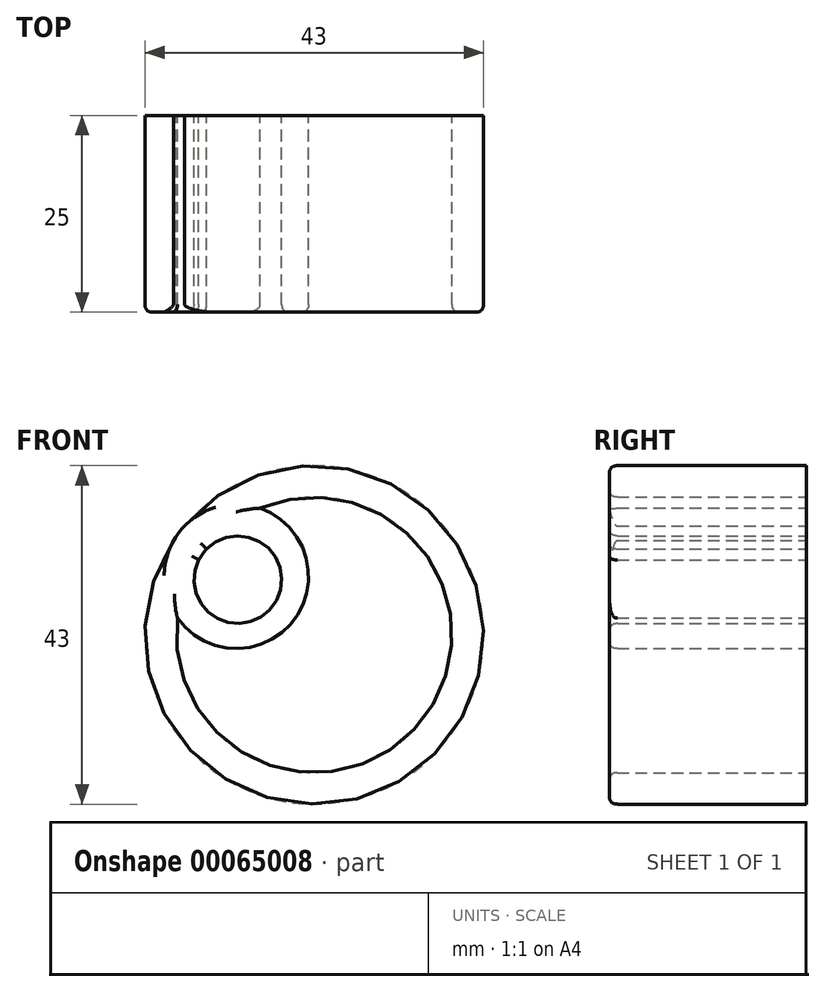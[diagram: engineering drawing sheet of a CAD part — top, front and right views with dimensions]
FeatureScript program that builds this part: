
annotation { "Feature Type Name" : "Feature", "Feature Type Description" : "" }
export const myFeature = defineFeature(function(context is Context, id is Id, definition is map)
    precondition{}
    {
        {
            var Q0;
            Q0=qCreatedBy(makeId("Front.planeOp"),FACE);
            var sketch = newSketch(context, id + "F0", { "sketchPlane" : qUnion([Q0])});
            skCircle(sketch, "E0", {"center": v(0, 0) * mm, "radius": 21.5 * mm});
            skCircle(sketch, "E1", {"center": v(0, 0) * mm, "radius": 17.5 * mm});
            skSolve(sketch);
        }
        {
            var Q0;
            Q0 = qSketchRegion(id + "F0", true);
            extrude(context, id + "F1", {"entities" : qUnion([Q0]), "depth" : 25 * mm});
        }
        {
            var Q0;
            Q0=qCreatedBy(makeId("Front.planeOp"),FACE);
            var sketch = newSketch(context, id + "F2", { "sketchPlane" : qUnion([Q0])});
            skCircle(sketch, "E2", {"center": v(-9.89, 7.43) * mm, "radius": 9.17 * mm});
            skPoint(sketch, "E2.first.point", {"position": v(-16.92, 13.32) * mm});
            skPoint(sketch, "E2.second.point", {"position": v(-1.16, 4.61) * mm});
            skPoint(sketch, "E2.third.point", {"position": v(-1.05, 4.98) * mm});
            skCircle(sketch, "E3", {"center": v(-9.7, 7.01) * mm, "radius": 5.57 * mm});
            skPoint(sketch, "E3.first.point", {"position": v(-14.32, 10.14) * mm});
            skPoint(sketch, "E3.second.point", {"position": v(-4.83, 4.31) * mm});
            skPoint(sketch, "E3.third.point", {"position": v(-4.24, 5.95) * mm});
            skSolve(sketch);
        }
        {
            var Q0;
            Q0 = qSketchRegion(id + "F2", true);
            extrude(context, id + "F3", {"entities" : qUnion([Q0]), "operationType" : NewBodyOperationType.ADD, "depth" : 25 * mm});
        }
        {
            var Q0;
            Q0=qCreatedBy(makeId("Front.planeOp"),FACE);
            var sketch = newSketch(context, id + "F4", { "sketchPlane" : qUnion([Q0])});
            skCircle(sketch, "E4", {"center": v(9.71, 7.92) * mm, "radius": 8.9 * mm});
            skPoint(sketch, "E4.first.point", {"position": v(15.77, 14.45) * mm});
            skPoint(sketch, "E4.second.point", {"position": v(4.3, 0.85) * mm});
            skPoint(sketch, "E4.third.point", {"position": v(1.12, 5.6) * mm});
            skCircle(sketch, "E5", {"center": v(9.55, 7.62) * mm, "radius": 5.27 * mm});
            skPoint(sketch, "E5.first.point", {"position": v(13.47, 11.14) * mm});
            skPoint(sketch, "E5.second.point", {"position": v(5.74, 3.97) * mm});
            skPoint(sketch, "E5.third.point", {"position": v(5.36, 4.4) * mm});
            skSolve(sketch);
        }
        {
            var Q0;
            Q0=sQuery(id+"F4.wireOp",EDGE,"E4");
            var Q1;
            Q1=sQuery(id+"F4.wireOp",EDGE,"E5");
            extrude(context, id + "F5", {"bodyType" : ToolBodyType.SURFACE, "surfaceEntities" : qUnion([Q0, Q1]), "depth" : 25 * mm});
        }
        {
            var Q0;
            Q0=makeQuery(id+"F3.opExtrude","CAP_EDGE",EDGE,{"disambiguationData":[OSD([sQuery(id+"F2.wireOp",EDGE,"E3")])],"isStart":false});
            var Q1;
            {var subQ0=sQuery(id+"F0.wireOp",EDGE,"E1");var subQ1=sQuery(id+"F2.wireOp",EDGE,"E2");Q1=makeQuery(id+"F3.boolean.opBoolean","SPLIT",EDGE,{"disambiguationData":[TD([makeQuery(id+"F3.opExtrude","SWEPT_FACE",FACE,{"disambiguationData":[OSD([subQ1])]})])],"derivedFrom":makeQuery(id+"F1.opExtrude","CAP_EDGE",EDGE,{"disambiguationData":[OSD([subQ0])],"isStart":false})});}
            var Q2;
            Q2=makeQuery(id+"F1.opExtrude","CAP_EDGE",EDGE,{"disambiguationData":[OSD([sQuery(id+"F0.wireOp",EDGE,"E0")])],"isStart":false});
            var Q3;
            {var subQ0=sQuery(id+"F0.wireOp",EDGE,"E1");var subQ1=sQuery(id+"F2.wireOp",EDGE,"E2");Q3=makeQuery(id+"F3.boolean.opBoolean","SPLIT",EDGE,{"disambiguationData":[TD([makeQuery(id+"F1.opExtrude","SWEPT_FACE",FACE,{"disambiguationData":[OSD([subQ0])]})])],"derivedFrom":makeQuery(id+"F3.opExtrude","CAP_EDGE",EDGE,{"disambiguationData":[OSD([subQ1])],"isStart":false})});}
            var Q4;
            {var subQ0=sQuery(id+"F0.wireOp",EDGE,"E1");var subQ1=sQuery(id+"F2.wireOp",EDGE,"E3");Q4=makeQuery(id+"F3.boolean.opBoolean","SPLIT",EDGE,{"disambiguationData":[TD([makeQuery(id+"F3.opExtrude","SWEPT_FACE",FACE,{"disambiguationData":[OSD([subQ1])]})])],"derivedFrom":makeQuery(id+"F1.opExtrude","CAP_EDGE",EDGE,{"disambiguationData":[OSD([subQ0])],"isStart":false})});}
            fillet(context, id + "F6", {"entities" : qUnion([Q0, Q1, Q2, Q3, Q4]), "radius" : 1 * mm, "tangentPropagation" : true, "rho" : 0.5, "crossSection" : FilletCrossSection.CONIC, "allowEdgeOverflow" : false});
        }
    });
